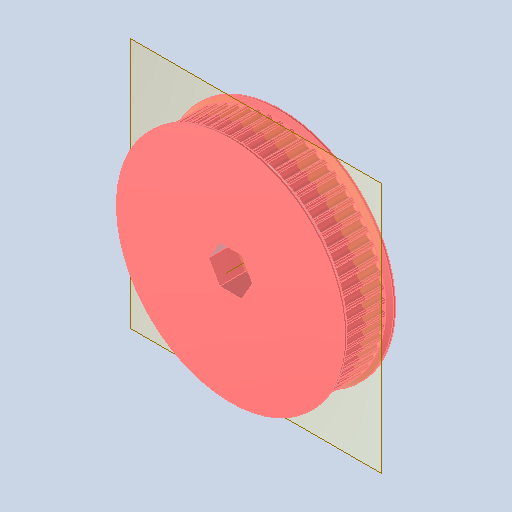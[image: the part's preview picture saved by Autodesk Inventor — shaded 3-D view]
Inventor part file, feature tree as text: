
AUTODESK INVENTOR PART (.ipt)
format: ipt  version: 2022.3 (Build 263350000, 350)  size: 504,320 bytes
history: native  units: in
note: dims shown in document units (in); Inventor stores cm internally (conversion verified against a paired STEP export)
features: sketch x7, extrude x6, mirror x2, chamfer x2, other x1, fillet x1, pattern_circular x1
ambient origin geometry x8: Origin, YZ Plane, XZ Plane, XY Plane, X Axis, Y Axis, Z Axis, Center Point
bodies: Solid1 (feature_tree)
feature tree (20):
  other  "Hex Bore"
  extrude  "HTD Base"  Depth=0.3937in TaperAngle=0.0deg
  extrude  "HTD Flange"  Depth=0.0591in
  mirror  "HTD Flanges"
  chamfer  "HTD Flange Chamfer"  Distance=0.0787in Angle=45.0deg
  extrude  "GT2 Base"  TaperAngle=0.0deg  [1 undecoded]
  extrude  "GT2 Base Tooth"  TaperAngle=0.0deg  [1 undecoded]
  fillet  "GT2 Base Tooth pt. 2"  Radius=2.2257in
  pattern_circular  "GT2 Teeth"  [2 undecoded]
  extrude  "GT2 Flange"  Depth=0.0591in
  mirror  "GT2 Flanges"
  chamfer  "GT2 Flange Chamfer"  Distance=0.0075in
  extrude  "Circle Bore"  TaperAngle=0.0deg  [1 undecoded]
  sketch  "Sketch1"  dims[d0=3.7146in d1=0.3937in d2=0.0in]
  sketch  "Sketch3"  dims[d12=0.0394in d13=0.0591in]
  sketch  "Sketch4"  dims[d14=0.0in]
  sketch  "Sketch5"  dims[d15=0.0394in d16=0.0787in d17=45.0deg]
  sketch  "Sketch6"  dims[d18=0.385in d19=0.0in d20=0.0in]
  sketch  "Sketch7"  dims[d21=0.385in d22=0.0in d23=0.0in d24=2.2257in]
  sketch  "Sketch8"  dims[d25=0.3937in d26=0.0in d27=0.0727in d28=0.0075in d29=0.0in d30=0.0in d31=0.0118in d32=23.622in d33=360.0deg d35=0.0394in d36=0.0591in d37=0.0in d38=0.0394in d39=0.0787in d40=45.0deg]
note: 5 required parameter values undecoded (feature->parameter linkage not recoverable at this tier; creation-order binding heuristic only, values carry confidence <= 0.55)
